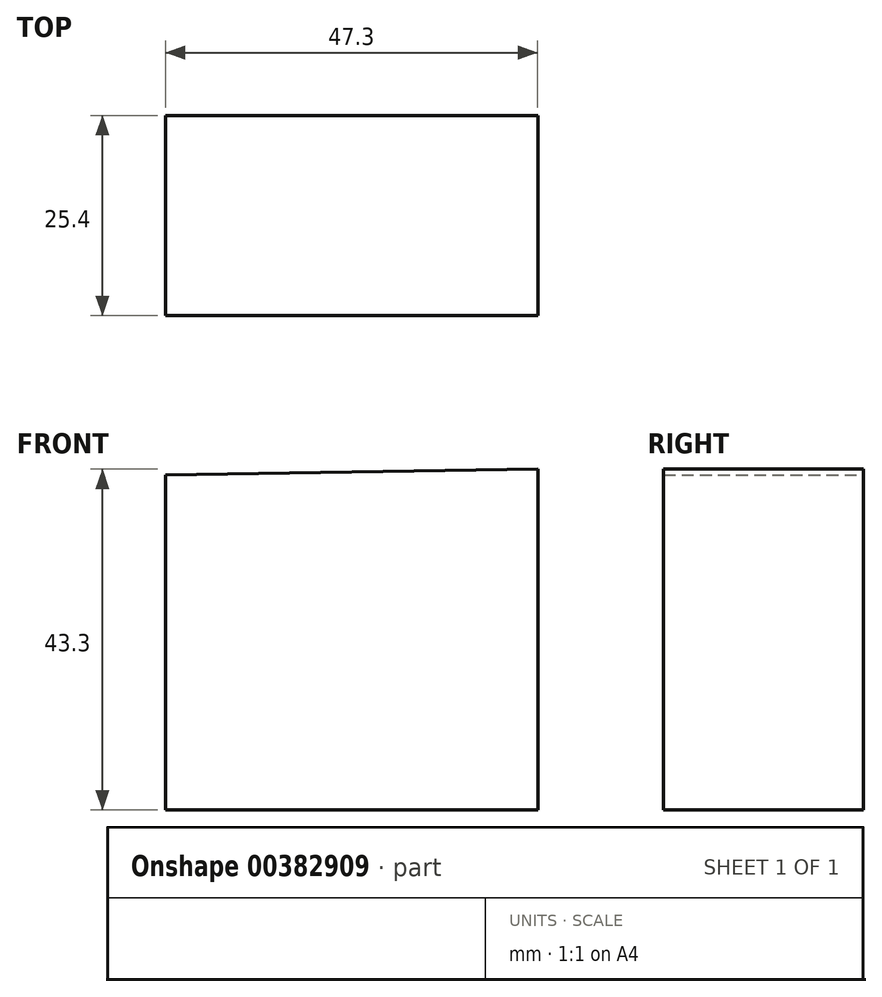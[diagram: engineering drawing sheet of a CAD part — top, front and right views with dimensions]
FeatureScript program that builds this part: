
annotation { "Feature Type Name" : "Feature", "Feature Type Description" : "" }
export const myFeature = defineFeature(function(context is Context, id is Id, definition is map)
    precondition{}
    {
        {
            var Q0;
            Q0=qCreatedBy(makeId("Front.planeOp"),FACE);
            var sketch = newSketch(context, id + "F0", { "sketchPlane" : qUnion([Q0])});
            skLineSegment(sketch, "E0", {"start": v(-22.89, 21.46) * mm, "end": v(-22.89, -21.08) * mm});
            skLineSegment(sketch, "E1", {"start": v(-22.89, -21.08) * mm, "end": v(24.41, -21.08) * mm});
            skLineSegment(sketch, "E2", {"start": v(24.41, -21.08) * mm, "end": v(24.41, 22.22) * mm});
            skLineSegment(sketch, "E3", {"start": v(24.41, 22.22) * mm, "end": v(-22.89, 21.46) * mm});
            skSolve(sketch);
        }
        {
            var Q0;
            Q0=makeQuery(id+"F0.imprint","IMPRINT",FACE,{"disambiguationData":[TD([[makeQuery(id+"F0.imprint","IMPRINT",EDGE,{"derivedFrom":sQuery(id+"F0.wireOp",EDGE,"E0")}),1.0]])]});
            var Q1;
            Q1=sQuery(id+"F0.wireOp",EDGE,"E3");
            var Q2;
            Q2=sQuery(id+"F0.wireOp",EDGE,"E0");
            var Q3;
            Q3=sQuery(id+"F0.wireOp",EDGE,"E1");
            var Q4;
            Q4=sQuery(id+"F0.wireOp",EDGE,"E2");
            extrude(context, id + "F1", {"entities" : qUnion([Q0]), "surfaceEntities" : qUnion([Q1, Q2, Q3, Q4]), "depth" : 25.4 * mm});
        }
    });
